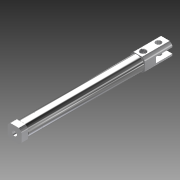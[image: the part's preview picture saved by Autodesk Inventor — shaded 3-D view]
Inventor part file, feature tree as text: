
AUTODESK INVENTOR PART (.ipt)
format: ipt  version: 2012 (Build 160160000, 160)  size: 177,664 bytes
history: native  units: in
note: dims shown in document units (in); Inventor stores cm internally (conversion verified against a paired STEP export)
features: sketch x2, other x1, imported_body x1, thread x1, hole x1, plane x1, split x1, move_body x1, extrude x1
ambient origin geometry x8: Origin, YZ Plane, XZ Plane, XY Plane, X Axis, Y Axis, Z Axis, Center Point
bodies: Solid2 (feature_tree), Solid3 (feature_tree)
feature tree (10):
  other  "D-ClevisPinDetail"
  imported_body  "Base1"
  thread  "Thread1"  [1 undecoded]
  hole  "Hole1"  [1 undecoded]
  plane  "Work Plane1"
  split  "Split1"
  move_body  "Move Body1"
  extrude  "Extrusion1"  Depth=1.0236in TaperAngle=0.0deg
  sketch  "Sketch1"  dims[d2=0.1882in d3=0.2362in d4=0.1575in d5=0.0787in d6=90.0deg d7=0.315in d8=0.8108in d9=-1.0in]
  sketch  "Sketch2"  dims[d10=0.0in d11=0.0in d12=0.75in d13=1.0236in d14=0.0in]
note: 2 required parameter values undecoded (feature->parameter linkage not recoverable at this tier; creation-order binding heuristic only, values carry confidence <= 0.55)
